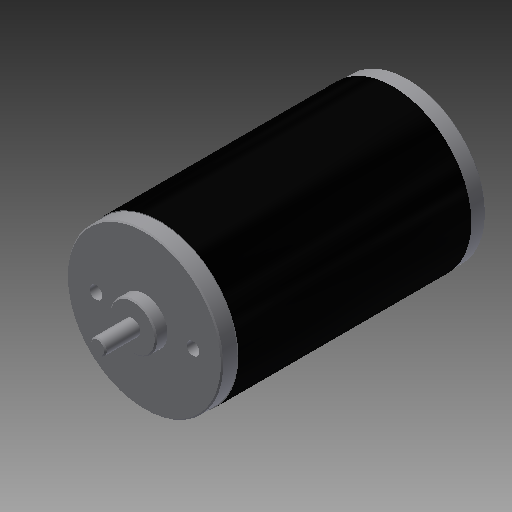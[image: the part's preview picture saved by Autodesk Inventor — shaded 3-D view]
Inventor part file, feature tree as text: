
AUTODESK INVENTOR PART (.ipt)
format: ipt  version: 2018 (Build 220112000, 112)  size: 145,920 bytes
history: native  units: in
note: dims shown in document units (in); Inventor stores cm internally (conversion verified against a paired STEP export)
features: chamfer x1, other x1, imported_body x1
ambient origin geometry x8: Origin, YZ Plane, XZ Plane, XY Plane, X Axis, Y Axis, Z Axis, Center Point
bodies: Body1 (feature_tree)
feature tree (3):
  chamfer  "Chamfer1"  [1 undecoded]
  other  "BAG Motor1"
  imported_body  "Base1"
note: 1 required parameter value undecoded (feature->parameter linkage not recoverable at this tier; creation-order binding heuristic only, values carry confidence <= 0.55)
